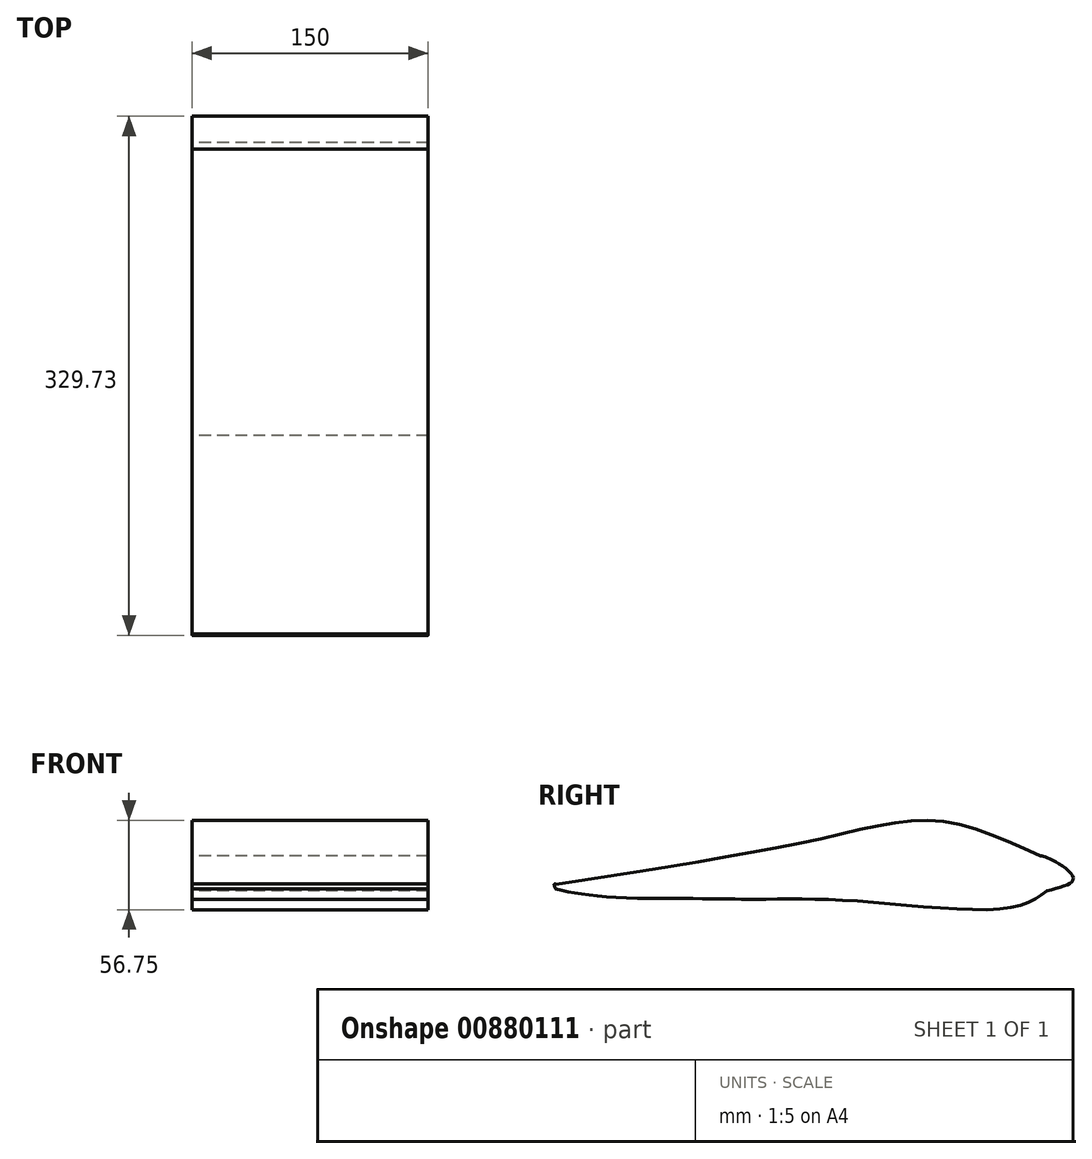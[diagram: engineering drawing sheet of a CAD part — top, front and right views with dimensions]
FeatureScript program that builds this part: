
annotation { "Feature Type Name" : "Feature", "Feature Type Description" : "" }
export const myFeature = defineFeature(function(context is Context, id is Id, definition is map)
    precondition{}
    {
        {
            var Q0;
            Q0=qCreatedBy(makeId("Right.planeOp"),FACE);
            var sketch = newSketch(context, id + "F0", { "sketchPlane" : qUnion([Q0])});
            skFitSpline(sketch, "E0", {"points": [v(-156.64, -23.94) * mm, v(-126.76, -28.68) * mm, v(-61.24, -30.06) * mm, v(-30.55, -30.58) * mm]});
            skFitSpline(sketch, "E1", {"points": [v(-30.55, -30.58) * mm, v(37.21, -31.73) * mm, v(132.4, -35.78) * mm, v(155.43, -25.02) * mm]});
            skFitSpline(sketch, "E2", {"points": [v(155.43, -25.02) * mm, v(172.18, -17.19) * mm, v(158.28, -5.25) * mm, v(151.15, -2.83) * mm]});
            skFitSpline(sketch, "E3", {"points": [v(151.15, -2.83) * mm, v(85.86, 19.32) * mm, v(12.16, 8.1) * mm, v(-156.53, -20.87) * mm]});
            skFitSpline(sketch, "E4", {"points": [v(-156.53, -20.87) * mm, v(-157.53, -21.04) * mm, v(-156.65, -23.9) * mm, v(-156.64, -23.94) * mm, v(-156.64, -23.94) * mm, v(-156.64, -23.94) * mm]});
            skLineSegment(sketch, "E5", {"start": v(163.36, -16.06) * mm, "end": v(163.36, -41.23) * mm, "construction": true});
            skSolve(sketch);
        }
        {
            var Q0;
            Q0=makeQuery(id+"F0.imprint","IMPRINT",FACE,{"disambiguationData":[TD([[makeQuery(id+"F0.imprint","IMPRINT",EDGE,{"derivedFrom":sQuery(id+"F0.wireOp",EDGE,"E0")}),1.0]])]});
            extrude(context, id + "F1", {"entities" : qUnion([Q0]), "depth" : 150 * mm, "offsetDistance" : 25 * mm});
        }
    });
